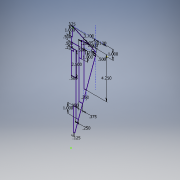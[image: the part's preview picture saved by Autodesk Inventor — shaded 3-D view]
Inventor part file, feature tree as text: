
AUTODESK INVENTOR PART (.ipt)
format: ipt  version: 2017 (Build 210142000, 142)  size: 124,416 bytes
history: native  units: in
note: dims shown in document units (in); Inventor stores cm internally (conversion verified against a paired STEP export)
features: sketch x1
ambient origin geometry x8: Origin, YZ Plane, XZ Plane, XY Plane, X Axis, Y Axis, Z Axis, Center Point
feature tree (1):
  sketch  "Sketch1"  dims[d0=1.13in d1=3.7in d2=0.125in d3=0.1718in d5=1.0in d6=1.0in d7=90.0deg d8=0.5in d9=15.0deg d12=1.25in d13=0.25in d16=0.5in d17=0.5in d18=0.5in d19=2.5in d20=0.5in d22=0.375in d23=0.25in d25=0.234in d26=15.0deg d27=0.125in d28=0.25in d29=1.0in d30=4.25in d31=0.25in d32=1.0in]
